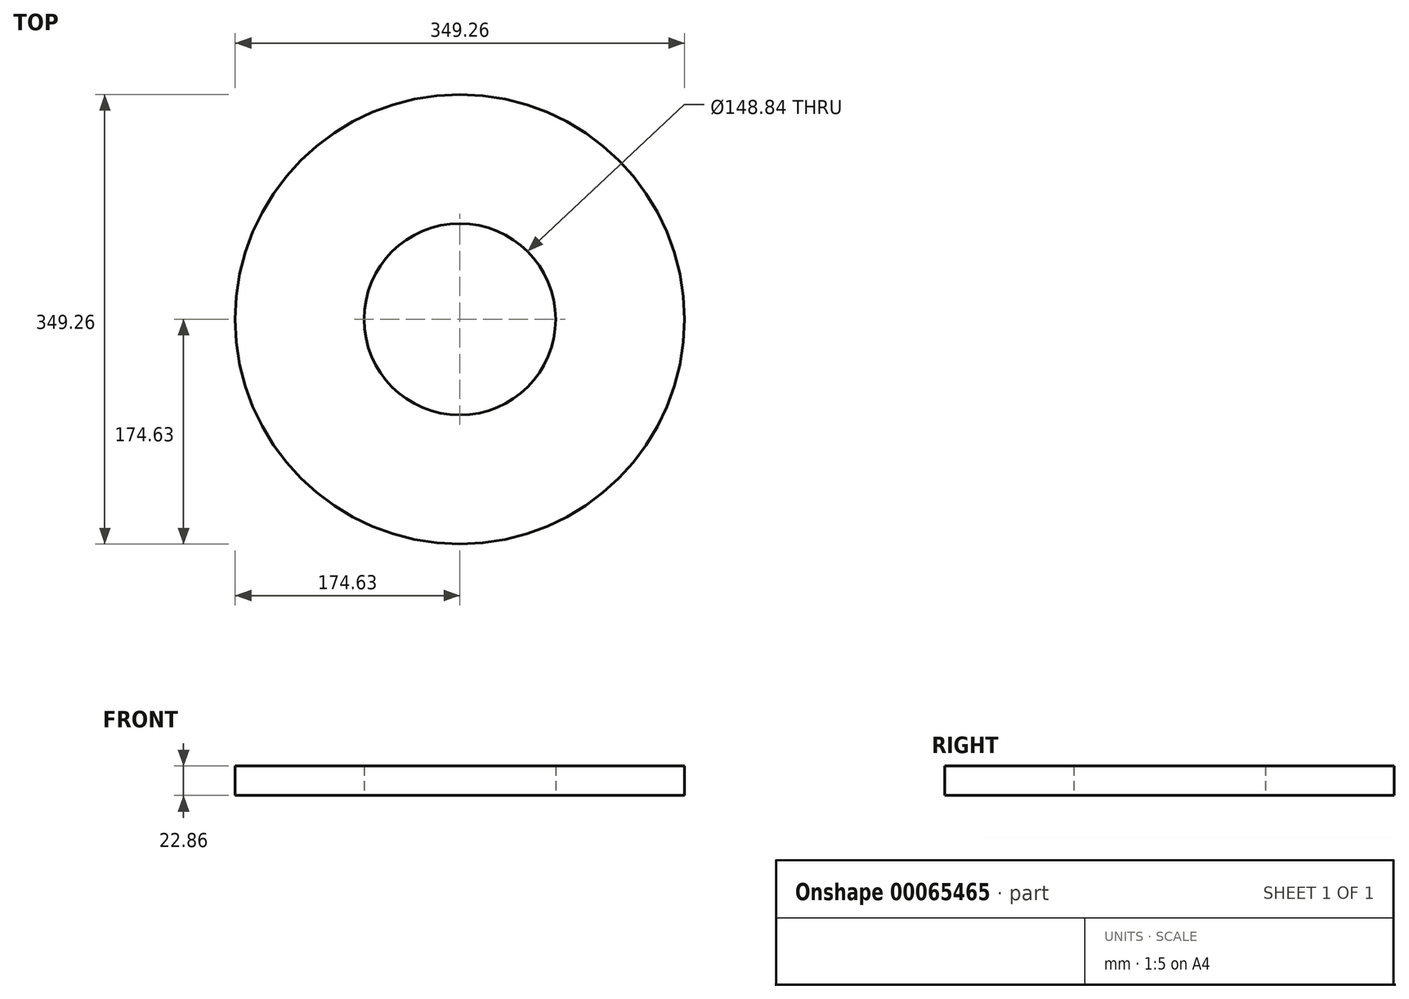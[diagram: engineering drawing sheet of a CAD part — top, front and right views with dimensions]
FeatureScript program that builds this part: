
annotation { "Feature Type Name" : "Feature", "Feature Type Description" : "" }
export const myFeature = defineFeature(function(context is Context, id is Id, definition is map)
    precondition{}
    {
        {
            var Q0;
            Q0=qCreatedBy(makeId("Top.planeOp"),FACE);
            var sketch = newSketch(context, id + "F0", { "sketchPlane" : qUnion([Q0])});
            skCircle(sketch, "E0", {"center": v(0, 0) * mm, "radius": 174.63 * mm});
            skCircle(sketch, "E1", {"center": v(0, 0) * mm, "radius": 74.42 * mm});
            skSolve(sketch);
        }
        {
            var Q0;
            Q0=makeQuery(id+"F0.imprint","IMPRINT",FACE,{"disambiguationData":[TD([[makeQuery(id+"F0.imprint","IMPRINT",EDGE,{"derivedFrom":sQuery(id+"F0.wireOp",EDGE,"E0")}),1.0]])]});
            extrude(context, id + "F1", {"entities" : qUnion([Q0]), "depth" : 22.86 * mm});
        }
    });
